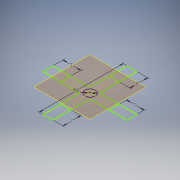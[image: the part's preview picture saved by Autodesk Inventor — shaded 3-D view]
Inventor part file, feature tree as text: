
AUTODESK INVENTOR PART (.ipt)
format: ipt  version: 2019 (Build 230136000, 136)  size: 100,352 bytes
history: native  units: in
note: dims shown in document units (in); Inventor stores cm internally (conversion verified against a paired STEP export)
features: sketch x1, plane x1
ambient origin geometry x8: Origin, YZ Plane, XZ Plane, XY Plane, X Axis, Y Axis, Z Axis, Center Point
feature tree (2):
  sketch  "草图1"  dims[d0=0.1575in d1=1.2992in d2=0.1575in d8=0.2756in d9=0.2756in d10=0.2756in d11=0.2756in]
  plane  "工作平面1"
